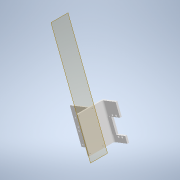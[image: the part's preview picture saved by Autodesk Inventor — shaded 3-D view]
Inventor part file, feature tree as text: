
AUTODESK INVENTOR PART (.ipt)
format: ipt  version: 2021 (Build 250183000, 183)  size: 202,752 bytes
history: native  units: mm
features: reference x11, other x9, sketch x7, extrude x2, plane x2, projected_geometry x2
ambient origin geometry x8: Origin, YZ Plane, XZ Plane, XY Plane, X Axis, Y Axis, Z Axis, Center Point
bodies: Solid1 (feature_tree)
feature tree (33):
  other  "servo_mount.ipt"
  extrude  "Extrusion1"  Depth=3.0mm
  extrude  "Extrusion2"  Depth=40.0mm TaperAngle=0.0deg
  other  "Solid1::servo_mount.ipt"
  other  "TaggingFeature1"
  sketch  "Sketch1"  dims[d0=10.0mm d1=3.0mm]
  sketch  "Sketch2"  dims[d2=55.0mm d3=0.0mm d4=40.0mm d5=0.0mm]
  sketch  "Sketch3"
  sketch  "Sketch4"
  sketch  "Sketch5"
  plane  "Work Plane1"
  plane  "Work Plane2"
  sketch  "Sketch6"
  projected_geometry  "Projected Loop1"
  reference  "Reference1"
  reference  "Reference2"
  sketch  "Sketch7"
  reference  "Reference3"
  reference  "Reference4"
  projected_geometry  "Projected Loop2"
  reference  "Reference5"
  reference  "Reference6"
  reference  "Reference7"
  reference  "Reference8"
  reference  "Reference9"
  reference  "Reference10"
  reference  "Reference11"
  other  "4_WheelsSwerve01.iam"
  other  "Part10"
  other  "MPU-9250:2"
  other  "board:1"
  other  "GPS_ublox_board:1"
  other  "HCM5883L:1"
